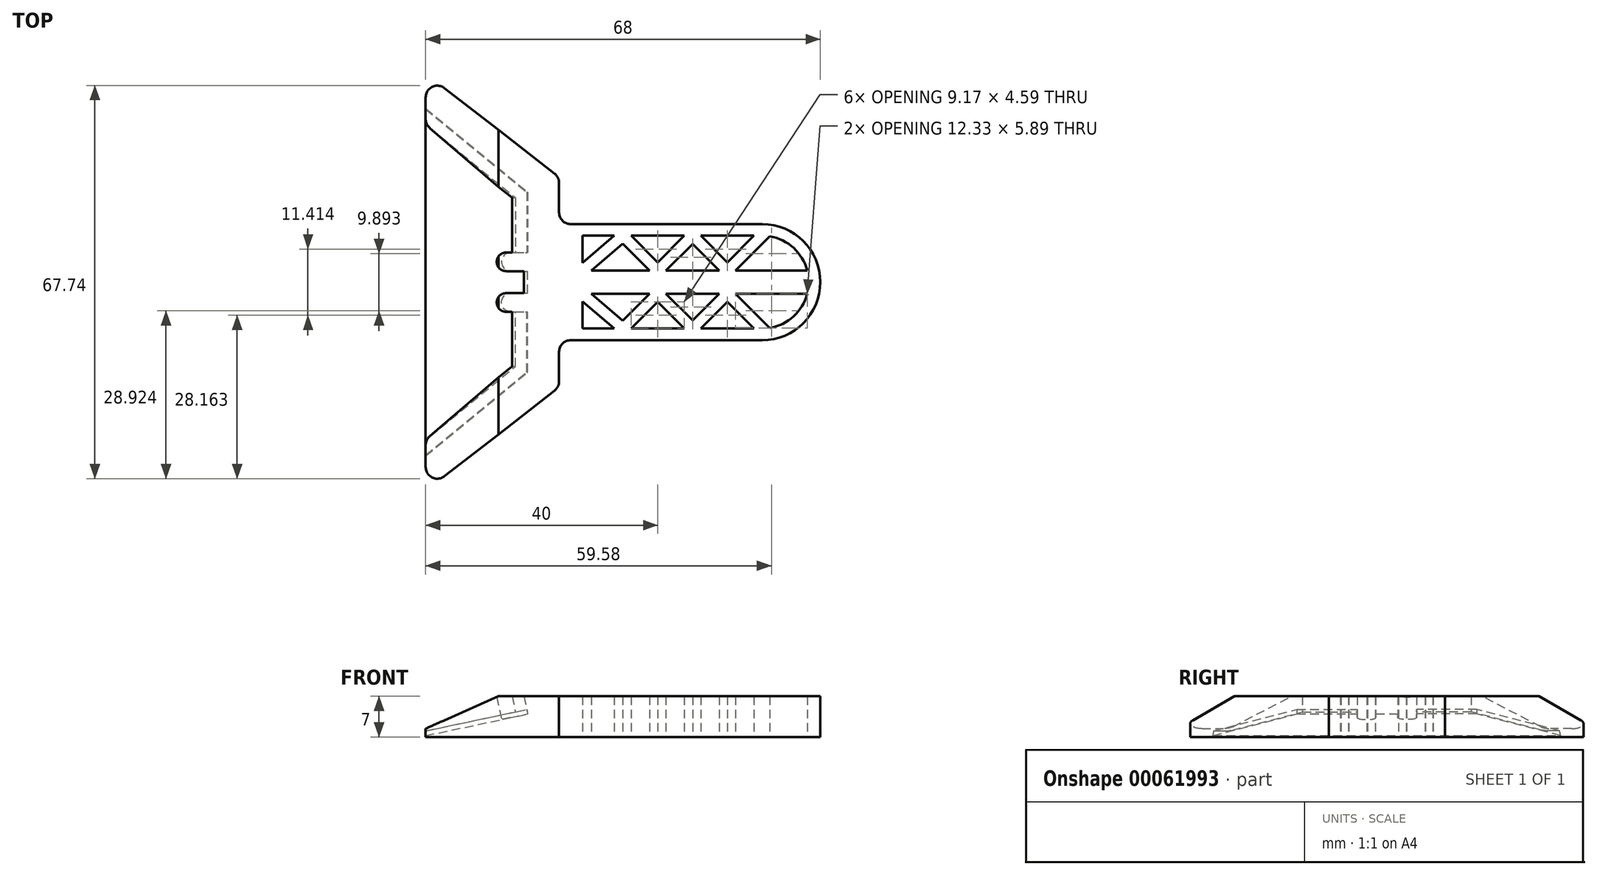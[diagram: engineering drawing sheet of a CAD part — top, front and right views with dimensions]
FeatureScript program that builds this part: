
annotation { "Feature Type Name" : "Feature", "Feature Type Description" : "" }
export const myFeature = defineFeature(function(context is Context, id is Id, definition is map)
    precondition{}
    {
        {
            var Q0;
            Q0=qCreatedBy(makeId("Top.planeOp"),FACE);
            var sketch = newSketch(context, id + "F0", { "sketchPlane" : qUnion([Q0])});
            skLineSegment(sketch, "E0", {"start": v(0, -36.73) * mm, "end": v(0, 49.06) * mm});
            skLineSegment(sketch, "E1", {"start": v(0, 0) * mm, "end": v(69, 0) * mm});
            skLineSegment(sketch, "E2.0", {"start": v(19, -15.65) * mm, "end": v(19, 0) * mm, "construction": true});
            skLineSegment(sketch, "E3", {"start": v(0, -30.4) * mm, "end": v(19, -15.65) * mm, "construction": true});
            skLineSegment(sketch, "E4.0", {"start": v(10.3, -3.25) * mm, "end": v(25.47, -3.25) * mm, "construction": true});
            skLineSegment(sketch, "E5.0", {"start": v(16, -30.4) * mm, "end": v(16, 8.04) * mm, "construction": true});
            skLineSegment(sketch, "E6.0", {"start": v(0, -36.73) * mm, "end": v(24, -18.1) * mm});
            skLineSegment(sketch, "E7.0", {"start": v(24, -18.1) * mm, "end": v(24, -10) * mm});
            skLineSegment(sketch, "E8.0", {"start": v(24, -10) * mm, "end": v(59, -10) * mm});
            skArc(sketch, "E9", {"start": v(59, -10) * mm, "mid": v(66.07, -7.07) * mm, "end": v(69, 0) * mm});
            skLineSegment(sketch, "E10.0", {"start": v(28.01, -8) * mm, "end": v(33.47, -8) * mm});
            skArc(sketch, "E11.0", {"start": v(60.3, -7.9) * mm, "mid": v(64.4, -5.9) * mm, "end": v(66.75, -2) * mm});
            skLineSegment(sketch, "E12.0", {"start": v(28.01, -8) * mm, "end": v(28.01, -3.32) * mm});
            skLineSegment(sketch, "E13.0", {"start": v(60.3, -7.9) * mm, "end": v(54.41, -2) * mm});
            skLineSegment(sketch, "E14.0", {"start": v(57.59, -8) * mm, "end": v(53, -3.41) * mm});
            skLineSegment(sketch, "E15.0", {"start": v(51.59, -2) * mm, "end": v(47, -6.59) * mm});
            skLineSegment(sketch, "E16.0", {"start": v(53, -3.41) * mm, "end": v(48.41, -8) * mm});
            skLineSegment(sketch, "E17.0", {"start": v(47, -6.59) * mm, "end": v(42.41, -2) * mm});
            skLineSegment(sketch, "E18.0", {"start": v(45.59, -8) * mm, "end": v(41, -3.41) * mm});
            skLineSegment(sketch, "E19.0", {"start": v(39.59, -2) * mm, "end": v(34.95, -6.64) * mm});
            skLineSegment(sketch, "E20.0", {"start": v(41, -3.41) * mm, "end": v(36.41, -8) * mm});
            skLineSegment(sketch, "E21.0", {"start": v(35, -6.68) * mm, "end": v(29.55, -2) * mm});
            skLineSegment(sketch, "E22.0", {"start": v(33.47, -8) * mm, "end": v(28.01, -3.32) * mm});
            skLineSegment(sketch, "E23.trimOffspring", {"start": v(68.8, -2) * mm, "end": v(69, -2) * mm});
            skLineSegment(sketch, "E24.trimOffspring", {"start": v(54.41, -2) * mm, "end": v(66.75, -2) * mm});
            skLineSegment(sketch, "E25.trimOffspring", {"start": v(42.41, -2) * mm, "end": v(51.59, -2) * mm});
            skLineSegment(sketch, "E26.trimOffspring", {"start": v(36.41, -8) * mm, "end": v(45.59, -8) * mm});
            skLineSegment(sketch, "E27.trimOffspring", {"start": v(48.41, -8) * mm, "end": v(57.59, -8) * mm});
            skLineSegment(sketch, "E28.trimOffspring", {"start": v(29.55, -2) * mm, "end": v(39.59, -2) * mm});
            skSolve(sketch);
        }
        {
            var Q0;
            {var subQ4=sQuery(id+"F0.wireOp",EDGE,"E1");Q0=makeQuery(id+"F0.imprint","IMPRINT",FACE,{"disambiguationData":[TD([[makeQuery(id+"F0.imprint","IMPRINT",EDGE,{"derivedFrom":subQ4}),-1.0]])]});}
            extrude(context, id + "F1", {"entities" : qUnion([Q0]), "depth" : 7 * mm});
        }
        {
            var Q0;
            Q0=makeQuery(id+"F1.opExtrude","SWEPT_FACE",FACE,{"disambiguationData":[OSD([sQuery(id+"F0.wireOp",EDGE,"E1")])]});
            var sketch = newSketch(context, id + "F2", { "sketchPlane" : qUnion([Q0])});
            skLineSegment(sketch, "E29.0", {"start": v(0, 4) * mm, "end": v(-69, 4) * mm});
            skLineSegment(sketch, "E30", {"start": v(0, 0) * mm, "end": v(-18.82, 4) * mm});
            skLineSegment(sketch, "E31.0", {"start": v(0.2, 0.98) * mm, "end": v(-18.61, 4.98) * mm, "construction": true});
            skLineSegment(sketch, "E32", {"start": v(0, 0.98) * mm, "end": v(-13.53, 7) * mm});
            skSolve(sketch);
        }
        {
            var Q0;
            Q0=makeQuery(id+"F1.opExtrude","CAP_EDGE",EDGE,{"disambiguationData":[OSD([sQuery(id+"F0.wireOp",EDGE,"E0")])],"isStart":true});
            var Q1;
            Q1=sQuery(id+"F2.wireOp",EDGE,"E30");
            cPlane(context, id + "F3", {"entities" : qUnion([Q0, Q1]), "cplaneType" : CPlaneType.LINE_ANGLE, "offset" : 150 * mm, "angle" : 0 * degree, "width" : 150 * mm, "height" : 150 * mm});
        }
        {
            var Q0;
            Q0=qCreatedBy(id+"F3.planeOp",FACE);
            var sketch = newSketch(context, id + "F4", { "sketchPlane" : qUnion([Q0])});
            skLineSegment(sketch, "E33.0", {"start": v(0, 30.75) * mm, "end": v(0, 0) * mm});
            skLineSegment(sketch, "E34.0", {"start": v(19, 15.5) * mm, "end": v(19, 5.1) * mm});
            skLineSegment(sketch, "E35.0", {"start": v(0, 30.75) * mm, "end": v(19.24, 30.75) * mm, "construction": true});
            skLineSegment(sketch, "E36.0", {"start": v(0, 15.5) * mm, "end": v(19.24, 15.5) * mm, "construction": true});
            skLineSegment(sketch, "E37", {"start": v(0, 30.75) * mm, "end": v(19, 15.5) * mm});
            skLineSegment(sketch, "E38.0", {"start": v(16, 8.54) * mm, "end": v(16, -3.4) * mm, "construction": true});
            skLineSegment(sketch, "E39.0", {"start": v(12.06, 3.5) * mm, "end": v(19.24, 3.5) * mm, "construction": true});
            skArc(sketch, "E40", {"start": v(16, 5.1) * mm, "mid": v(14.4, 3.5) * mm, "end": v(16, 1.9) * mm});
            skPoint(sketch, "E41.orphan", {"position": v(0, 36.73) * mm});
            skLineSegment(sketch, "E42", {"start": v(19, 0) * mm, "end": v(0, 0) * mm});
            skPoint(sketch, "E43.orphan", {"position": v(0, -49.06) * mm});
            skLineSegment(sketch, "E44", {"start": v(16, 5.1) * mm, "end": v(19, 5.1) * mm});
            skLineSegment(sketch, "E45", {"start": v(16, 1.9) * mm, "end": v(19, 1.9) * mm});
            skLineSegment(sketch, "E46.trimOffspring", {"start": v(19, 1.9) * mm, "end": v(19, 0) * mm});
            skLineSegment(sketch, "E47.0", {"start": v(17, 14.54) * mm, "end": v(17, 5.1) * mm});
            skLineSegment(sketch, "E48.0", {"start": v(0, 28.19) * mm, "end": v(17, 14.54) * mm});
            skSolve(sketch);
        }
        {
            var Q0;
            Q0=makeQuery(id+"F4.imprint","IMPRINT",FACE,{"disambiguationData":[TD([[makeQuery(id+"F4.imprint","IMPRINT",EDGE,{"derivedFrom":sQuery(id+"F4.wireOp",EDGE,"E33.0")}),1.0]])]});
            extrude(context, id + "F5", {"entities" : qUnion([Q0]), "operationType" : NewBodyOperationType.REMOVE, "oppositeDirection" : true, "depth" : 0.8 * mm});
        }
        {
            var Q0;
            {var subQ1=sQuery(id+"F4.wireOp",EDGE,"E40");Q0=makeQuery(id+"F4.imprint","IMPRINT",FACE,{"disambiguationData":[TD([[makeQuery(id+"F4.imprint","IMPRINT",EDGE,{"derivedFrom":subQ1}),-1.0]])]});}
            var Q1;
            Q1=makeQuery(id+"F1.opExtrude","CAP_FACE",FACE,{"disambiguationData":[OSD([sQuery(id+"F0.wireOp",EDGE,"E0"),sQuery(id+"F0.wireOp",EDGE,"E1"),sQuery(id+"F0.wireOp",EDGE,"E6.0"),sQuery(id+"F0.wireOp",EDGE,"E7.0"),sQuery(id+"F0.wireOp",EDGE,"E8.0"),sQuery(id+"F0.wireOp",EDGE,"E9"),sQuery(id+"F0.wireOp",EDGE,"E10.0"),sQuery(id+"F0.wireOp",EDGE,"E11.0"),sQuery(id+"F0.wireOp",EDGE,"E12.0"),sQuery(id+"F0.wireOp",EDGE,"E13.0"),sQuery(id+"F0.wireOp",EDGE,"E14.0"),sQuery(id+"F0.wireOp",EDGE,"E15.0"),sQuery(id+"F0.wireOp",EDGE,"E16.0"),sQuery(id+"F0.wireOp",EDGE,"E17.0"),sQuery(id+"F0.wireOp",EDGE,"E18.0"),sQuery(id+"F0.wireOp",EDGE,"E19.0"),sQuery(id+"F0.wireOp",EDGE,"E20.0"),sQuery(id+"F0.wireOp",EDGE,"E21.0"),sQuery(id+"F0.wireOp",EDGE,"E22.0"),sQuery(id+"F0.wireOp",EDGE,"E24.trimOffspring"),sQuery(id+"F0.wireOp",EDGE,"E25.trimOffspring"),sQuery(id+"F0.wireOp",EDGE,"E26.trimOffspring"),sQuery(id+"F0.wireOp",EDGE,"E27.trimOffspring"),sQuery(id+"F0.wireOp",EDGE,"E28.trimOffspring")])],"isStart":false});
            extrude(context, id + "F6", {"entities" : qUnion([Q0]), "operationType" : NewBodyOperationType.REMOVE, "endBound" : BoundingType.UP_TO_SURFACE, "oppositeDirection" : true, "endBoundEntityFace" : qUnion([Q1]), "depth" : 25 * mm});
        }
        {
            var Q0;
            Q0=makeQuery(id+"F1.opExtrude","SWEPT_FACE",FACE,{"disambiguationData":[OSD([sQuery(id+"F0.wireOp",EDGE,"E0")])]});
            var sketch = newSketch(context, id + "F7", { "sketchPlane" : qUnion([Q0])});
            skLineSegment(sketch, "E49.bottom", {"start": v(36.73, 7) * mm, "end": v(0, 7) * mm});
            skLineSegment(sketch, "E49.top", {"start": v(36.73, 0) * mm, "end": v(0, 0) * mm});
            skLineSegment(sketch, "E49.left", {"start": v(36.73, 7) * mm, "end": v(36.73, 0) * mm});
            skLineSegment(sketch, "E49.right", {"start": v(0, 7) * mm, "end": v(0, 0) * mm});
            skSolve(sketch);
        }
        {
            var Q0;
            Q0 = qSketchRegion(id + "F7", true);
            extrude(context, id + "F8", {"entities" : qUnion([Q0]), "operationType" : NewBodyOperationType.REMOVE, "oppositeDirection" : true, "depth" : 1 * mm});
        }
        {
            var Q0;
            {var subQ0=sQuery(id+"F2.wireOp",EDGE,"E29.0");var subQ3=sQuery(id+"F2.wireOp",EDGE,"E32");var subQ4=makeQuery(id+"F2.imprint","INTERSECT",VERTEX,{"derivedFrom":[subQ0,subQ3]});Q0=makeQuery(id+"F2.imprint","IMPRINT",FACE,{"disambiguationData":[TD([[makeQuery(id+"F2.imprint","IMPRINT",EDGE,{"disambiguationData":[TD([[subQ4,1.0]])],"derivedFrom":subQ0}),1.0]])]});}
            var Q1;
            {var subQ1=sQuery(id+"F0.wireOp",EDGE,"E1");var subQ4=sQuery(id+"F2.wireOp",EDGE,"E32");var subQ6=makeQuery(id+"F1.opExtrude","CAP_EDGE",EDGE,{"disambiguationData":[OSD([subQ1])],"isStart":false});var subQ8=makeQuery(id+"F2.imprint","INTERSECT",VERTEX,{"derivedFrom":[subQ6,subQ4]});Q1=makeQuery(id+"F2.imprint","IMPRINT",FACE,{"disambiguationData":[TD([[makeQuery(id+"F2.imprint","IMPRINT",EDGE,{"disambiguationData":[TD([[subQ8,1.0]])],"derivedFrom":subQ4}),-1.0]])]});}
            extrude(context, id + "F9", {"entities" : qUnion([Q0, Q1]), "operationType" : NewBodyOperationType.REMOVE, "oppositeDirection" : true, "depth" : 45 * mm});
        }
        {
            var Q0;
            Q0=makeQuery(id+"F8.boolean.opBoolean","INTERSECT",EDGE,{"derivedFrom":[makeQuery(id+"F1.opExtrude","SWEPT_FACE",FACE,{"disambiguationData":[OSD([sQuery(id+"F0.wireOp",EDGE,"E6.0")])]}),makeQuery(id+"F8.opExtrude","CAP_FACE",FACE,{"disambiguationData":[OSD([sQuery(id+"F7.wireOp",EDGE,"E49.bottom"),sQuery(id+"F7.wireOp",EDGE,"E49.top"),sQuery(id+"F7.wireOp",EDGE,"E49.left"),sQuery(id+"F7.wireOp",EDGE,"E49.right")])],"isStart":false})]});
            var Q1;
            Q1=makeQuery(id+"F1.opExtrude","SWEPT_EDGE",EDGE,{"disambiguationData":[OSD([sQuery(id+"F0.wireOp",EDGE,"E6.0"),sQuery(id+"F0.wireOp",EDGE,"E7.0")])]});
            var Q2;
            Q2=makeQuery(id+"F1.opExtrude","SWEPT_EDGE",EDGE,{"disambiguationData":[OSD([sQuery(id+"F0.wireOp",EDGE,"E7.0"),sQuery(id+"F0.wireOp",EDGE,"E8.0")])]});
            var Q3;
            {var subQ0=sQuery(id+"F0.wireOp",EDGE,"E6.0");var subQ1=sQuery(id+"F0.wireOp",EDGE,"E1");var subQ2=sQuery(id+"F2.wireOp",EDGE,"E32");Q3=makeQuery(id+"F9.boolean.opBoolean","COPY",EDGE,{"disambiguationData":[TD([makeQuery(id+"F1.opExtrude","SWEPT_FACE",FACE,{"disambiguationData":[OSD([subQ0])]})])],"derivedFrom":makeQuery(id+"F9.opExtrude","SWEPT_EDGE",EDGE,{"disambiguationData":[OSD([subQ1,subQ2])]})});}
            var Q4;
            Q4=makeQuery(id+"F8.boolean.opBoolean","INTERSECT",EDGE,{"derivedFrom":[makeQuery(id+"F6.boolean.opBoolean","COPY",FACE,{"derivedFrom":makeQuery(id+"F6.opExtrude","SWEPT_FACE",FACE,{"disambiguationData":[OSD([sQuery(id+"F4.wireOp",EDGE,"E48.0")])]})}),makeQuery(id+"F8.opExtrude","CAP_FACE",FACE,{"disambiguationData":[OSD([sQuery(id+"F7.wireOp",EDGE,"E49.bottom"),sQuery(id+"F7.wireOp",EDGE,"E49.top"),sQuery(id+"F7.wireOp",EDGE,"E49.left"),sQuery(id+"F7.wireOp",EDGE,"E49.right")])],"isStart":false})]});
            fillet(context, id + "F10", {"entities" : qUnion([Q0, Q1, Q2, Q3, Q4]), "radius" : 2 * mm, "tangentPropagation" : true, "allowEdgeOverflow" : false});
        }
        {
            var Q0;
            Q0=makeQuery(id+"F1.opExtrude","SWEPT_BODY",BODY,{"disambiguationData":[OSD([sQuery(id+"F0.wireOp",EDGE,"E0"),sQuery(id+"F0.wireOp",EDGE,"E1"),sQuery(id+"F0.wireOp",EDGE,"E6.0"),sQuery(id+"F0.wireOp",EDGE,"E7.0"),sQuery(id+"F0.wireOp",EDGE,"E8.0"),sQuery(id+"F0.wireOp",EDGE,"E9"),sQuery(id+"F0.wireOp",EDGE,"E10.0"),sQuery(id+"F0.wireOp",EDGE,"E11.0"),sQuery(id+"F0.wireOp",EDGE,"E12.0"),sQuery(id+"F0.wireOp",EDGE,"E13.0"),sQuery(id+"F0.wireOp",EDGE,"E14.0"),sQuery(id+"F0.wireOp",EDGE,"E15.0"),sQuery(id+"F0.wireOp",EDGE,"E16.0"),sQuery(id+"F0.wireOp",EDGE,"E17.0"),sQuery(id+"F0.wireOp",EDGE,"E18.0"),sQuery(id+"F0.wireOp",EDGE,"E19.0"),sQuery(id+"F0.wireOp",EDGE,"E20.0"),sQuery(id+"F0.wireOp",EDGE,"E21.0"),sQuery(id+"F0.wireOp",EDGE,"E22.0"),sQuery(id+"F0.wireOp",EDGE,"E24.trimOffspring"),sQuery(id+"F0.wireOp",EDGE,"E25.trimOffspring"),sQuery(id+"F0.wireOp",EDGE,"E26.trimOffspring"),sQuery(id+"F0.wireOp",EDGE,"E27.trimOffspring"),sQuery(id+"F0.wireOp",EDGE,"E28.trimOffspring")])]});
            var Q1;
            Q1=qCreatedBy(makeId("Front.planeOp"),FACE);
            mirror(context, id + "F11", {"operationType" : NewBodyOperationType.ADD, "entities" : qUnion([Q0]), "mirrorPlane" : qUnion([Q1])});
        }
    });
